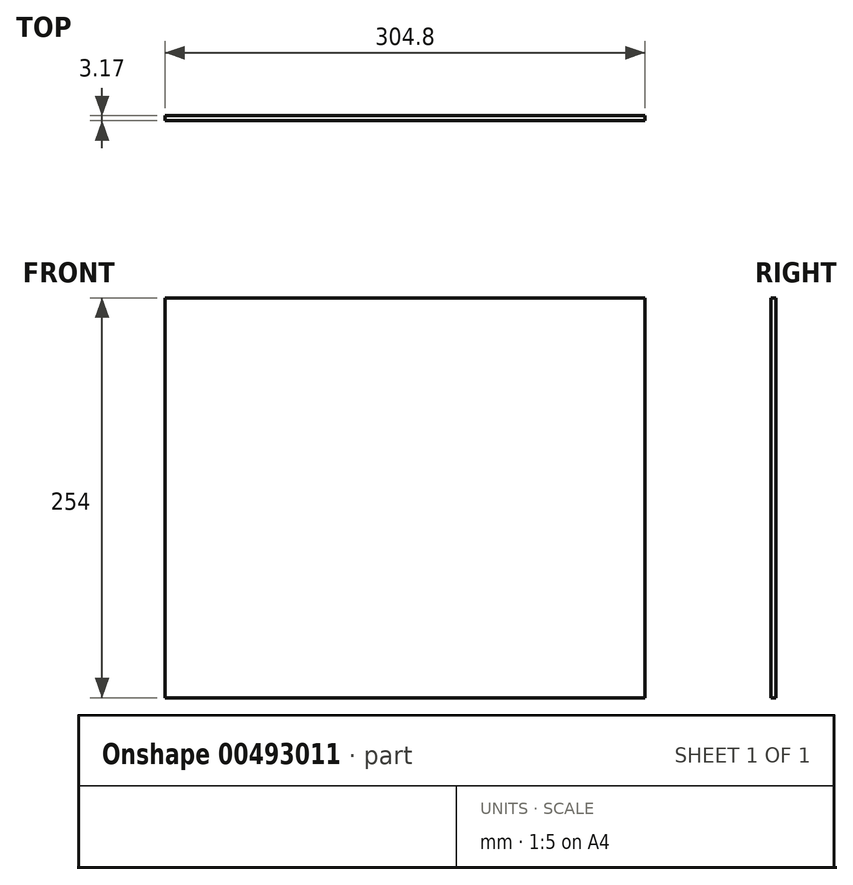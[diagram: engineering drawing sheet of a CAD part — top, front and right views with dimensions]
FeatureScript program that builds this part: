
annotation { "Feature Type Name" : "Feature", "Feature Type Description" : "" }
export const myFeature = defineFeature(function(context is Context, id is Id, definition is map)
    precondition{}
    {
        {
            var Q0;
            Q0=qCreatedBy(makeId("Front.planeOp"),FACE);
            var sketch = newSketch(context, id + "F0", { "sketchPlane" : qUnion([Q0])});
            skLineSegment(sketch, "E0.bottom", {"start": v(-152.4, 127) * mm, "end": v(152.4, 127) * mm});
            skLineSegment(sketch, "E0.top", {"start": v(-152.4, -127) * mm, "end": v(152.4, -127) * mm});
            skLineSegment(sketch, "E0.left", {"start": v(-152.4, 127) * mm, "end": v(-152.4, -127) * mm});
            skLineSegment(sketch, "E0.right", {"start": v(152.4, 127) * mm, "end": v(152.4, -127) * mm});
            skPoint(sketch, "E0.middle", {"position": v(0, 0) * mm});
            skSolve(sketch);
        }
        {
            var Q0;
            Q0=makeQuery(id+"F0.imprint","IMPRINT",FACE,{"disambiguationData":[TD([[makeQuery(id+"F0.imprint","IMPRINT",EDGE,{"derivedFrom":sQuery(id+"F0.wireOp",EDGE,"E0.bottom")}),-1.0]])]});
            extrude(context, id + "F1", {"entities" : qUnion([Q0]), "depth" : 3.17 * mm});
        }
    });
